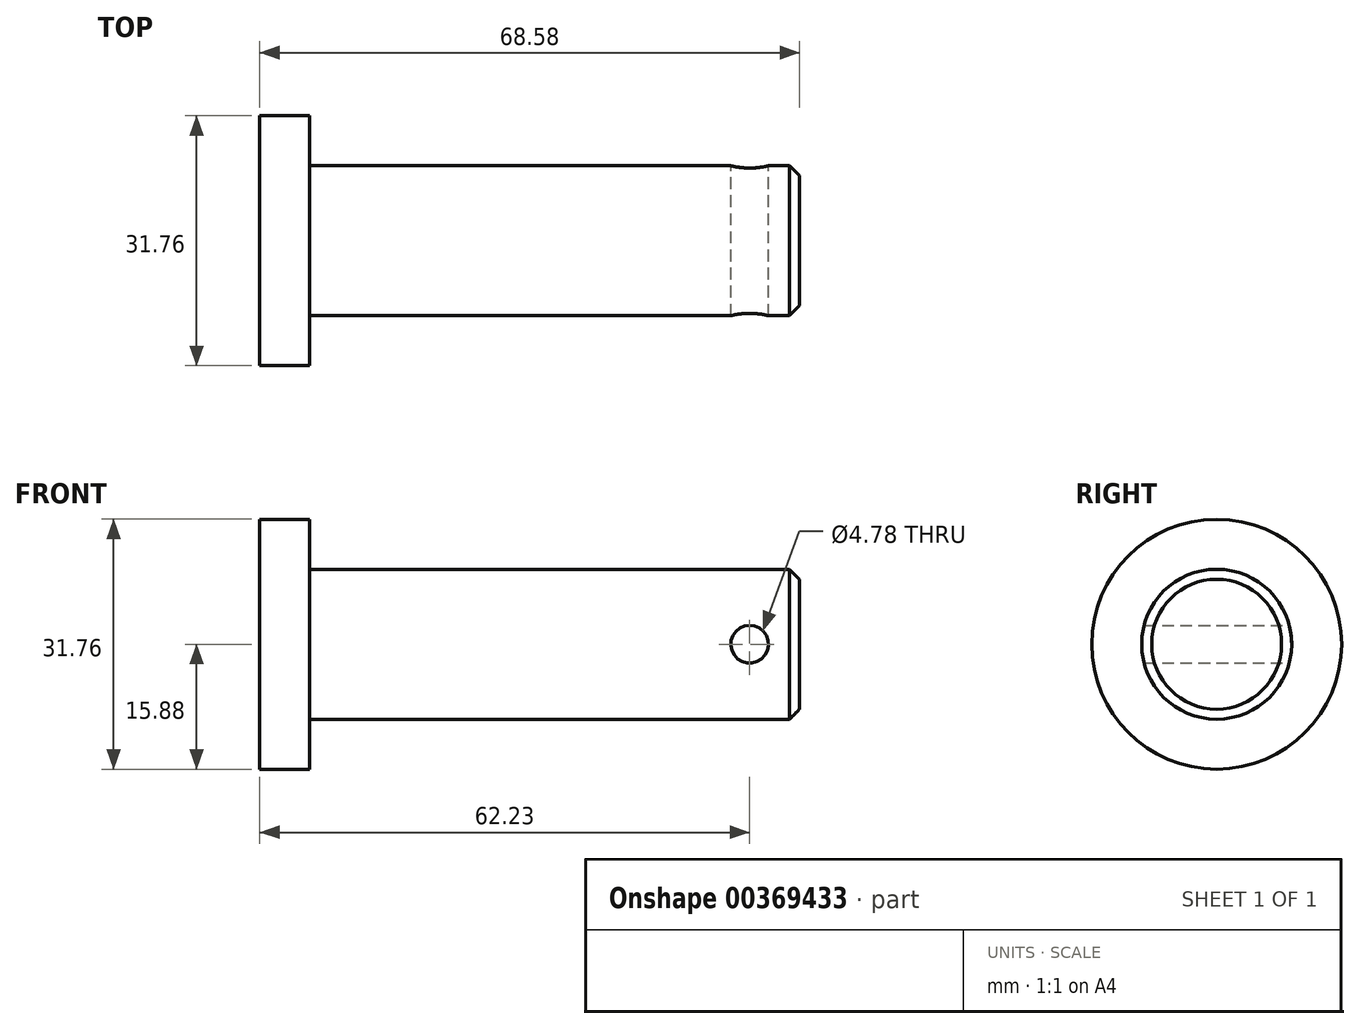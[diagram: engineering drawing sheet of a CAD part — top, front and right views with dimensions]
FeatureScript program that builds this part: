
annotation { "Feature Type Name" : "Feature", "Feature Type Description" : "" }
export const myFeature = defineFeature(function(context is Context, id is Id, definition is map)
    precondition{}
    {
        {
            var Q0;
            Q0=qCreatedBy(makeId("Right.planeOp"),FACE);
            var sketch = newSketch(context, id + "F0", { "sketchPlane" : qUnion([Q0])});
            skCircle(sketch, "E0", {"center": v(0, 0) * mm, "radius": 15.88 * mm});
            skSolve(sketch);
        }
        {
            var Q0;
            Q0 = qSketchRegion(id + "F0", true);
            extrude(context, id + "F1", {"entities" : qUnion([Q0]), "oppositeDirection" : true, "depth" : 6.35 * mm});
        }
        {
            var Q0;
            Q0=makeQuery(id+"F1.opExtrude","CAP_FACE",FACE,{"disambiguationData":[OSD([sQuery(id+"F0.wireOp",EDGE,"E0")])],"isStart":true});
            var sketch = newSketch(context, id + "F2", { "sketchPlane" : qUnion([Q0])});
            skCircle(sketch, "E1", {"center": v(0, 0) * mm, "radius": 9.53 * mm});
            skSolve(sketch);
        }
        {
            var Q0;
            Q0=makeQuery(id+"F2.imprint","IMPRINT",FACE,{"disambiguationData":[TD([[makeQuery(id+"F2.imprint","IMPRINT",EDGE,{"derivedFrom":sQuery(id+"F2.wireOp",EDGE,"E1")}),1.0]])]});
            extrude(context, id + "F3", {"entities" : qUnion([Q0]), "operationType" : NewBodyOperationType.ADD, "depth" : 62.23 * mm});
        }
        {
            var Q0;
            Q0=makeQuery(id+"F3.opExtrude","CAP_EDGE",EDGE,{"disambiguationData":[OSD([sQuery(id+"F2.wireOp",EDGE,"E1")])],"isStart":false});
            chamfer(context, id + "F4", {"entities" : qUnion([Q0]), "chamferType" : ChamferType.OFFSET_ANGLE, "width" : 1.27 * mm, "oppositeDirection" : false, "angle" : 45 * degree, "tangentPropagation" : true});
        }
        {
            var Q0;
            Q0=qCreatedBy(makeId("Front.planeOp"),FACE);
            var sketch = newSketch(context, id + "F5", { "sketchPlane" : qUnion([Q0])});
            skCircle(sketch, "E2", {"center": v(55.88, 0) * mm, "radius": 2.39 * mm});
            skSolve(sketch);
        }
        {
            var Q0;
            Q0 = qSketchRegion(id + "F5", true);
            extrude(context, id + "F6", {"entities" : qUnion([Q0]), "operationType" : NewBodyOperationType.REMOVE, "endBound" : BoundingType.SYMMETRIC, "depth" : 38.6 * mm});
        }
    });
